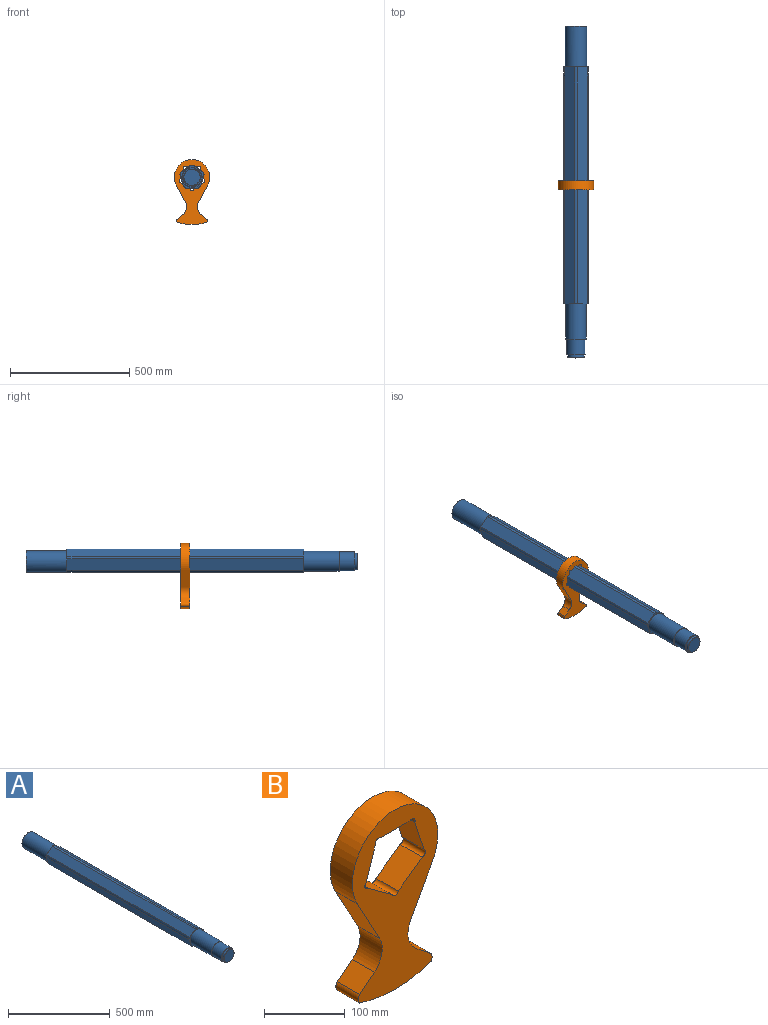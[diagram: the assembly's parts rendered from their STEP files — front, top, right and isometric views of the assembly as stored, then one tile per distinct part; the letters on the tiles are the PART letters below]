
ASSEMBLY  parts=2 mates=2
PART A: 30 faces, bbox 101.7x1393.5x97.2 mm
  f0: plane 42.8x31.09mm, normal (0,1,0), area 176.9mm2, adj f8,f22,f25,f29
  f1: plane 42.8x31.09mm, normal (0,1,0), area 176.9mm2, adj f4,f22,f28,f29
  f2: plane 50.31x24.23mm, normal (0,1,0), area 176.9mm2, adj f5,f22,f27,f28
  f3: plane 52.9x15.32mm, normal (0,1,0), area 176.9mm2, adj f6,f22,f26,f27
  f4: cylinder r=51.73mm len=992.5mm, axis (0,1,0), area 11554.5mm2, adj f1,f10,f28,f29
  f5: cylinder r=51.73mm len=992.5mm, axis (0,1,0), area 11554.5mm2, adj f2,f11,f27,f28
  f6: cylinder r=51.73mm len=992.5mm, axis (0,1,0), area 11554.5mm2, adj f3,f12,f26,f27
  f7: cylinder r=51.73mm len=992.5mm, axis (0,1,0), area 11554.5mm2, adj f13,f14,f25,f26
  f8: cylinder r=51.73mm len=992.5mm, axis (0,1,0), area 11554.5mm2, adj f0,f23,f25,f29
  f9: plane 100.73x96.23mm, normal (0,-1,0), area 1540.7mm2, adj f10,f11,f12,f13,f15,f23,f25,f26
  f10: cone r=51.73mm half-angle=45deg, axis (0,1,0), area 8.8mm2, adj f4,f9,f28,f29
  f11: cone r=51.73mm half-angle=45deg, axis (0,1,0), area 8.8mm2, adj f5,f9,f27,f28
  f12: cone r=51.73mm half-angle=45deg, axis (0,1,0), area 8.8mm2, adj f6,f9,f26,f27
  f13: cone r=51.73mm half-angle=45deg, axis (0,1,0), area 8.8mm2, adj f7,f9,f25,f26
  f14: plane 50.31x24.23mm, normal (0,1,0), area 176.9mm2, adj f7,f22,f25,f26
  f15: cylinder r=42.5mm len=148.9mm, axis (0,1,0), area 39761.6mm2, adj f9,f16
  f16: plane 85x85mm, normal (0,-1,0), area 710.6mm2, adj f15,f17
  f17: cylinder r=39.75mm len=79.5mm, axis (0,1,0), area 16683.7mm2, adj f16,f18
  f18: plane 79.5x79.5mm, normal (0,-1,0), area 1115.5mm2, adj f17,f19
  f19: cylinder r=35mm len=70mm, axis (0,1,0), area 2595mm2, adj f18,f24
  f20: plane 68x68mm, normal (0,-1,0), area 3631.7mm2, adj f24
  f21: plane 90x90mm, normal (0,1,0), area 6361.7mm2, adj f22
  f22: cylinder r=45mm len=172mm, axis (0,1,0), area 48631.9mm2, adj f0,f1,f2,f3,f14,f21
  f23: cone r=51.73mm half-angle=45deg, axis (0,1,0), area 8.8mm2, adj f8,f9,f25,f29
  f24: cone r=35mm half-angle=45deg, axis (0,1,0), area 306.6mm2, adj f19,f20
  f25: plane 993.01x48.54mm, normal (-0.95,0,-0.31), area 50671.4mm2, adj f0,f7,f8,f9,f13,f14,f23
  f26: plane 993.01x41.29mm, normal (-0.59,0,0.81), area 50671.4mm2, adj f3,f6,f7,f9,f12,f13,f14
  f27: plane 993.01x41.29mm, normal (0.59,0,0.81), area 50671.4mm2, adj f2,f3,f5,f6,f9,f11,f12
  f28: plane 993.01x48.54mm, normal (0.95,0,-0.31), area 50671.4mm2, adj f1,f2,f4,f5,f9,f10,f11
  f29: plane 993.01x51.04mm, normal (0,0,-1), area 50671.4mm2, adj f0,f1,f4,f8,f9,f10,f23
PART B: 22 faces, bbox 150x39x273 mm
  f0: cylinder r=5.65mm len=39mm, axis (0,1,0), area 553.4mm2, adj f1,f19,f20,f21
  f1: plane 49.56x39mm, normal (0.95,0,-0.31), area 2032.5mm2, adj f0,f2,f20,f21
  f2: cylinder r=5.65mm len=39mm, axis (0,1,0), area 553.4mm2, adj f1,f3,f20,f21
  f3: plane 52.12x39mm, normal (0,0,-1), area 2032.5mm2, adj f2,f4,f20,f21
  f4: cylinder r=5.65mm len=39mm, axis (0,1,0), area 553.4mm2, adj f3,f5,f20,f21
  f5: plane 49.56x39mm, normal (-0.95,0,-0.31), area 2032.5mm2, adj f4,f6,f20,f21
  f6: cylinder r=5.65mm len=39mm, axis (0,1,0), area 553.4mm2, adj f5,f7,f20,f21
  f7: plane 42.16x39mm, normal (-0.59,0,0.81), area 2032.5mm2, adj f6,f8,f20,f21
  f8: cylinder r=5.65mm len=39mm, axis (0,1,0), area 553.4mm2, adj f7,f19,f20,f21
  f9: cylinder r=9.54mm len=39mm, axis (0,1,0), area 551.2mm2, adj f10,f18,f20,f21
  f10: plane 39x26.07mm, normal (0.62,0,0.78), area 1302.2mm2, adj f9,f11,f20,f21
  f11: cylinder r=37.11mm len=46.68mm, axis (0,1,0), area 2016.7mm2, adj f10,f12,f20,f21
  f12: plane 71.67x39mm, normal (0.88,0,-0.48), area 3180.6mm2, adj f11,f13,f20,f21
  f13: cylinder r=75mm len=150mm, axis (0,1,0), area 12099.1mm2, adj f12,f14,f20,f21
  f14: plane 71.67x39mm, normal (-0.88,0,-0.48), area 3180.6mm2, adj f13,f15,f20,f21
  f15: cylinder r=37.11mm len=46.68mm, axis (0,1,0), area 2016.7mm2, adj f14,f16,f20,f21
  f16: plane 39x26.07mm, normal (-0.62,0,0.78), area 1302.2mm2, adj f15,f17,f20,f21
  f17: cylinder r=9.54mm len=39mm, axis (0,1,0), area 551.2mm2, adj f16,f18,f20,f21
  f18: cylinder r=198mm len=125mm, axis (0,1,0), area 4959.8mm2, adj f9,f17,f20,f21
  f19: plane 42.16x39mm, normal (0.59,0,0.81), area 2032.5mm2, adj f0,f8,f20,f21
  f20: plane 273x150mm, normal (0,-1,0), area 20209.1mm2, adj f0,f1,f2,f3,f4,f5,f6,f7
  f21: plane 273x150mm, normal (0,1,0), area 20209.1mm2, adj f0,f1,f2,f3,f4,f5,f6,f7
PLACE A t=(-150,-39,46.54)mm fixed
PLACE B t=(-150,705.51,46.54)mm
MATE slider A.f28 <-> B.f1  axis (0.95,0,-0.31) through (-107.2,686.01,32.64)mm
MATE slider B.f3 <-> A.f29  axis (0,0,-1) through (-150,686.01,91.54)mm
